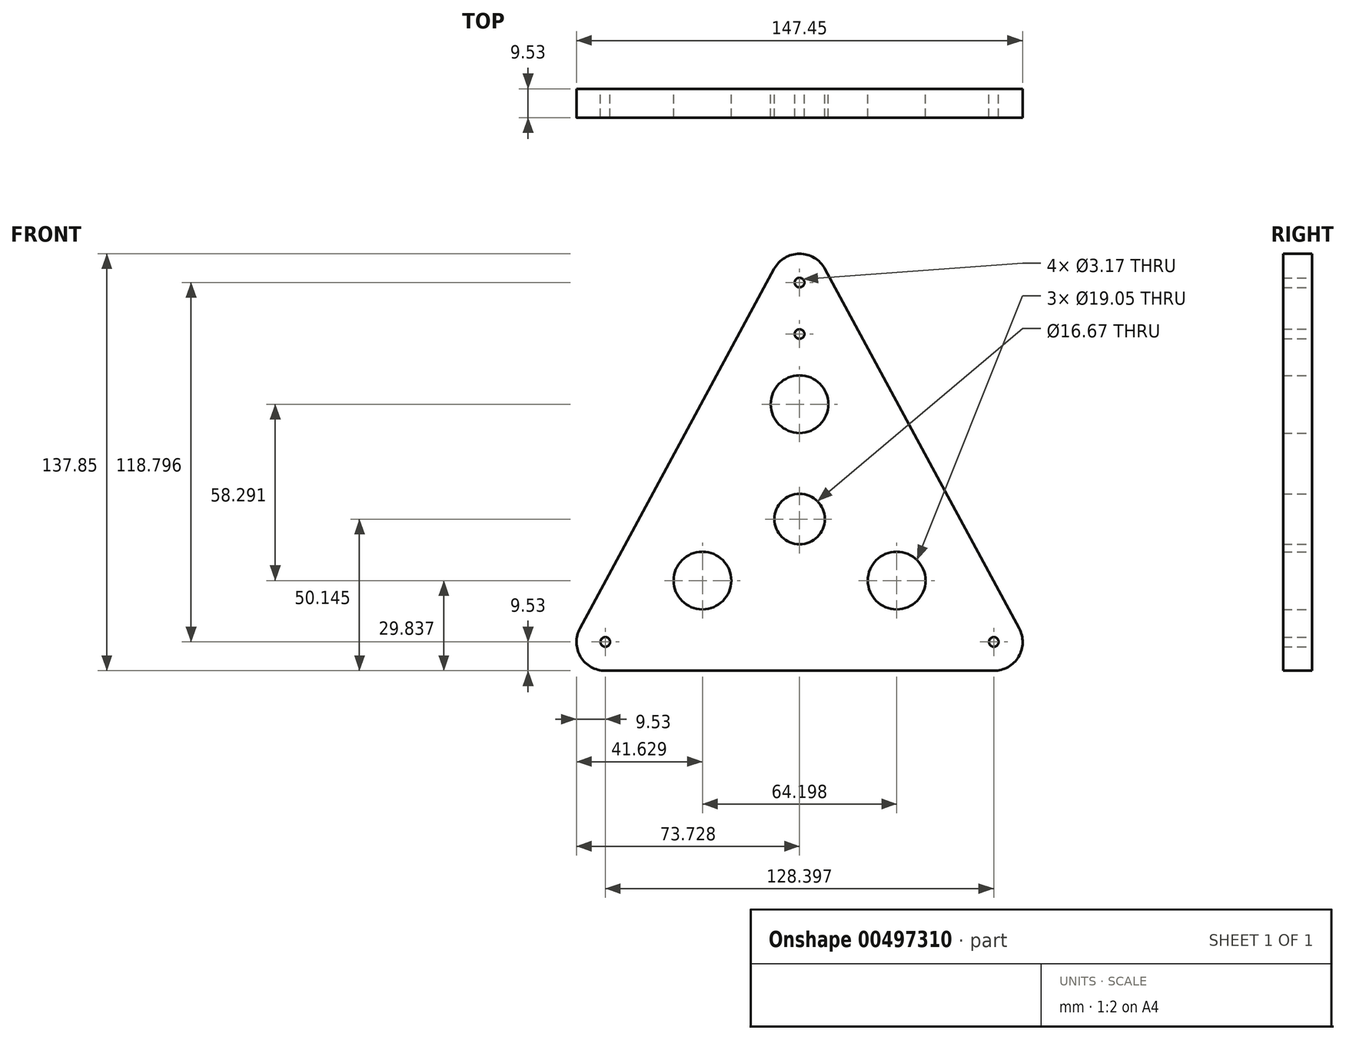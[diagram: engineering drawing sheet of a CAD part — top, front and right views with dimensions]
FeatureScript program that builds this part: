
annotation { "Feature Type Name" : "Feature", "Feature Type Description" : "" }
export const myFeature = defineFeature(function(context is Context, id is Id, definition is map)
    precondition{}
    {
        {
            var Q0;
            Q0=qCreatedBy(makeId("Front.planeOp"),FACE);
            var sketch = newSketch(context, id + "F0", { "sketchPlane" : qUnion([Q0])});
            skArc(sketch, "E0", {"start": v(72.58, 123.32) * mm, "mid": v(64.2, 128.32) * mm, "end": v(55.82, 123.32) * mm});
            skArc(sketch, "E1", {"start": v(-8.38, 4.53) * mm, "mid": v(-8.18, -4.88) * mm, "end": v(0, -9.53) * mm});
            skArc(sketch, "E2", {"start": v(128.4, -9.53) * mm, "mid": v(136.58, -4.88) * mm, "end": v(136.78, 4.53) * mm});
            skLineSegment(sketch, "E3", {"start": v(72.58, 123.32) * mm, "end": v(136.78, 4.53) * mm});
            skLineSegment(sketch, "E4", {"start": v(55.82, 123.32) * mm, "end": v(-8.38, 4.53) * mm});
            skLineSegment(sketch, "E5", {"start": v(128.4, -9.53) * mm, "end": v(0, -9.53) * mm});
            skCircle(sketch, "E6", {"center": v(64.2, 40.61) * mm, "radius": 8.33 * mm});
            skCircle(sketch, "E7", {"center": v(64.2, 118.8) * mm, "radius": 1.59 * mm});
            skCircle(sketch, "E8", {"center": v(0, 0) * mm, "radius": 1.59 * mm});
            skCircle(sketch, "E9", {"center": v(128.4, 0) * mm, "radius": 1.59 * mm});
            skLineSegment(sketch, "E10", {"start": v(64.2, 118.8) * mm, "end": v(64.2, 40.61) * mm, "construction": true});
            skLineSegment(sketch, "E11", {"start": v(64.2, 40.61) * mm, "end": v(0, 0) * mm, "construction": true});
            skLineSegment(sketch, "E12", {"start": v(128.4, 0) * mm, "end": v(0, 0) * mm, "construction": true});
            skLineSegment(sketch, "E13", {"start": v(64.2, 40.61) * mm, "end": v(128.4, 0) * mm, "construction": true});
            skCircle(sketch, "E14", {"center": v(32.1, 20.3) * mm, "radius": 9.53 * mm});
            skCircle(sketch, "E15", {"center": v(96.3, 20.3) * mm, "radius": 9.53 * mm});
            skCircle(sketch, "E16", {"center": v(64.2, 101.78) * mm, "radius": 1.59 * mm});
            skCircle(sketch, "E17", {"center": v(64.2, 78.6) * mm, "radius": 9.53 * mm});
            skSolve(sketch);
        }
        {
            var Q0;
            Q0=makeQuery(id+"F0.imprint","IMPRINT",FACE,{"disambiguationData":[TD([[makeQuery(id+"F0.imprint","IMPRINT",EDGE,{"derivedFrom":sQuery(id+"F0.wireOp",EDGE,"E0")}),1.0]])]});
            extrude(context, id + "F1", {"entities" : qUnion([Q0]), "depth" : 9.52 * mm});
        }
    });
